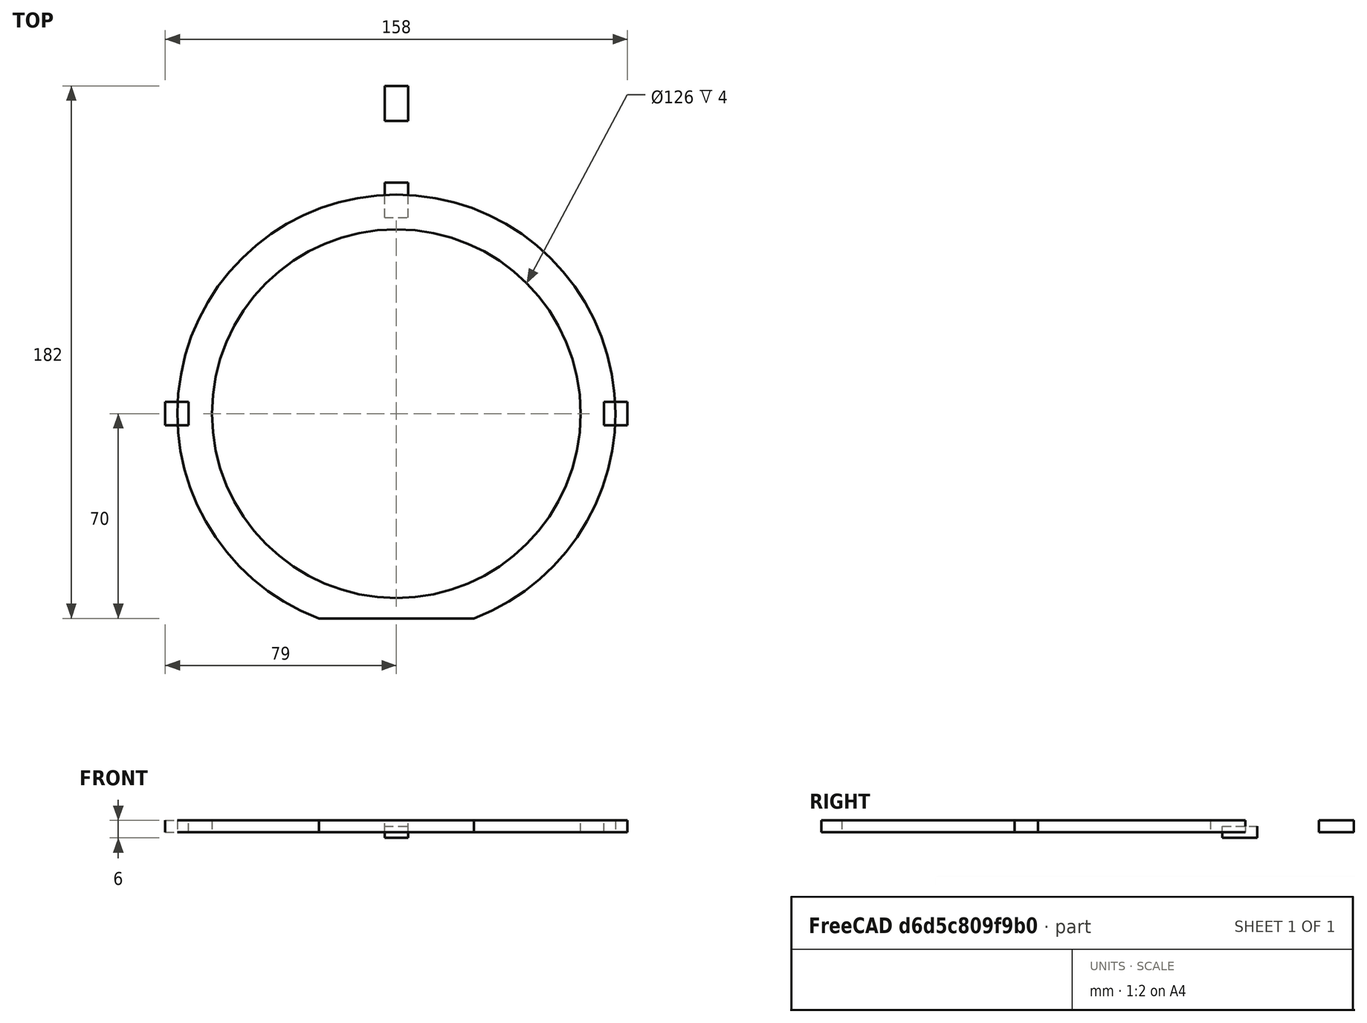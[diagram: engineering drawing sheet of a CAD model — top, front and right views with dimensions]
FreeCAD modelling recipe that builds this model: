
FCSTD DOCUMENT  (FreeCAD 0.19R0.19.2)
Label: waferHolder_003
License: All rights reserved
LicenseURL: http://en.wikipedia.org/wiki/All_rights_reserved
objects: Part::Box×4, Sketcher::SketchObject×1, Part::Extrusion×1
note: 6 computed .brp shape members not serialized (recipe doc carries the construction recipe); baked Part::Feature solids carry a one-line shape summary decoded from their .brp

FEATURE [Sketcher::SketchObject] Sketch
  FullyConstrained = true
  sketch-geometry (3):
    g0: Circle CenterX=-3.1415e-12 CenterY=5.6243e-12 CenterZ=0 NormalX=0 NormalY=0 NormalZ=1 AngleXU=0 Radius=63
    g1: ArcOfCircle CenterX=-3.1415e-12 CenterY=5.6243e-12 CenterZ=0 NormalX=0 NormalY=0 NormalZ=1 AngleXU=0 Radius=74.8482 StartAngle=5.07429 EndAngle=10.6337
    g2: LineSegment StartX=-26.5 StartY=-70.0001 StartZ=0 EndX=26.5 EndY=-70.0001 EndZ=0
  constraints (6):
    c: Block(g0)
    c: Coincident(g1,g0)
    c: Block(g1)
    c: Coincident(g2,g1)
    c: Coincident(g2,g1)
    c: Horizontal(g2)
FEATURE [Part::Box] Box  label="holderBitLeft"
  AttacherType = Attacher::AttachEngine3D
  Height = 4
  Length = 8
  Placement = pos=(-79,-4,0) rot=(0,0,1;0rad)
  Width = 8
FEATURE [Part::Box] Box001  label="bitHolderTopCutout"
  AttacherType = Attacher::AttachEngine3D
  Height = 4
  Length = 8
  Placement = pos=(-4,67,-2) rot=(0,0,1;0rad)
  Width = 12
FEATURE [Part::Extrusion] Extrude  label="mainHolderRing"
  Base = -> Sketch
  Dir = (0,0,1)
  DirMode = 2
  FaceMakerClass = Part::FaceMakerBullseye
  LengthFwd = 4
  LengthRev = 0
  Solid = true
  Symmetric = false
FEATURE [Part::Box] Box002  label="holderBitRight"
  AttacherType = Attacher::AttachEngine3D
  Height = 4
  Length = 8
  Placement = pos=(71,-4,0) rot=(0,0,1;0rad)
  Width = 8
FEATURE [Part::Box] Box003  label="bitHolderTop"
  AttacherType = Attacher::AttachEngine3D
  Height = 4
  Length = 8
  Placement = pos=(-4,100,0) rot=(0,0,1;0rad)
  Width = 12
